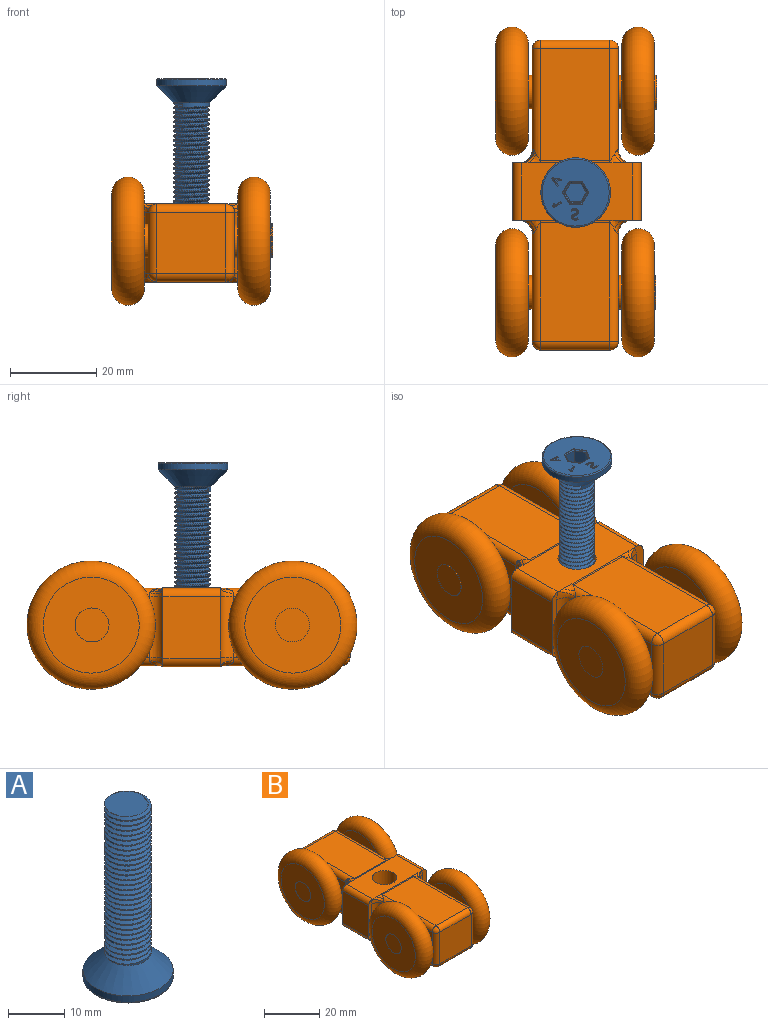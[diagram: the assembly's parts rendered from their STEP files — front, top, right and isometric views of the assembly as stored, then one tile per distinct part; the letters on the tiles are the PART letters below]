
ASSEMBLY  parts=2 mates=1
PART A: 134 faces, bbox 17.9x17.9x39 mm
  f0: plane 8.28x8.14mm, normal (0,0,1), area 47.4mm2, adj f4,f5,f7,f8
  f1: cylinder r=8.06mm len=16.12mm, axis (0,0,-1), area 70.4mm2, adj f3,f127
  f2: plane 15.61x15.61mm, normal (0,0,-1), area 159.1mm2, adj f49,f50,f51,f52,f53,f54,f55,f56
  f3: cone r=4.16mm half-angle=45deg, axis (0,0,-1), area 211.7mm2, adj f1,f4,f9
  f4: cylinder r=4.16mm len=32.5mm, axis (0,0,-1), area 180mm2, adj f0,f3,f5,f6,f7,f8
  f5: plane 0.02x0.01mm, normal (0.87,0.5,0), area 0mm2, adj f0,f4,f8
  f6: plane 0.84x0.63mm, normal (-0.87,-0.5,0), area 0.3mm2, adj f4,f7,f8,f9
  f7: bspline ~32.56x9.6mm, area 589mm2, adj f0,f4,f6,f8
  f8: bspline ~32.92x9.6mm, area 595.5mm2, adj f0,f4,f5,f6,f7,f9
  f9: cylinder r=4.16mm len=0.22mm, axis (0,0,-1), area 0mm2, adj f3,f6,f8
  f10: plane 3.14x2.29mm, normal (-0.86,0.5,0), area 8.3mm2, adj f11,f15,f22,f28
  f11: plane 3.14x2.31mm, normal (-0.87,-0.5,0), area 8.4mm2, adj f10,f12,f20,f26
  f12: plane 3.14x2.65mm, normal (0,-1,0), area 8.3mm2, adj f11,f13,f18,f24
  f13: plane 3.14x2.29mm, normal (0.86,-0.5,0), area 8.3mm2, adj f12,f14,f17,f23
  f14: plane 3.14x2.31mm, normal (0.87,0.5,0), area 8.4mm2, adj f13,f15,f19,f25
  f15: plane 3.14x2.65mm, normal (0,1,0), area 8.3mm2, adj f10,f14,f21,f27
  f16: plane 4.85x4.2mm, normal (0,0,-1), area 15.3mm2, adj f23,f24,f25,f26,f27,f28
  f17: plane 2.55x1.63mm, normal (0.61,-0.36,-0.71), area 1mm2, adj f13,f18,f19,f128
  f18: plane 2.95x0.26mm, normal (0,-0.71,-0.71), area 1mm2, adj f12,f17,f20,f130
  f19: plane 2.56x1.63mm, normal (0.61,0.35,-0.71), area 1mm2, adj f14,f17,f21,f129
  f20: plane 2.56x1.63mm, normal (-0.61,-0.35,-0.71), area 1mm2, adj f11,f18,f22,f132
  f21: plane 2.94x0.26mm, normal (0,0.71,-0.71), area 1mm2, adj f15,f19,f22,f131
  f22: plane 2.55x1.63mm, normal (-0.61,0.36,-0.71), area 1mm2, adj f10,f20,f21,f133
  f23: plane 2.29x1.45mm, normal (0.61,-0.36,-0.71), area 0.7mm2, adj f13,f16,f24,f25
  f24: plane 2.65x0.21mm, normal (0,-0.71,-0.71), area 0.7mm2, adj f12,f16,f23,f26
  f25: plane 2.31x1.45mm, normal (0.61,0.35,-0.71), area 0.7mm2, adj f14,f16,f23,f27
  f26: plane 2.31x1.45mm, normal (-0.61,-0.35,-0.71), area 0.7mm2, adj f11,f16,f24,f28
  f27: plane 2.65x0.21mm, normal (0,0.71,-0.71), area 0.7mm2, adj f15,f16,f25,f28
  f28: plane 2.29x1.45mm, normal (-0.61,0.36,-0.71), area 0.7mm2, adj f10,f16,f26,f27
  f29: plane 0.43x0.2mm, normal (-0.87,-0.5,0), area 0.1mm2, adj f30,f41,f42,f49
  f30: plane 1.65x1.32mm, normal (0.78,-0.62,0), area 0.9mm2, adj f29,f31,f42,f51
  f31: plane 0.43x0.17mm, normal (0.87,0.5,0), area 0.1mm2, adj f30,f32,f42,f53
  f32: plane 2.09x0.43mm, normal (-0.15,0.99,0), area 0.9mm2, adj f31,f33,f42,f55
  f33: plane 0.43x0.2mm, normal (-0.87,-0.5,0), area 0.1mm2, adj f32,f34,f42,f56
  f34: plane 0.66x0.43mm, normal (0.15,-0.99,0), area 0.3mm2, adj f33,f35,f42,f54
  f35: plane 0.68x0.43mm, normal (-0.87,-0.5,0), area 0.3mm2, adj f34,f41,f42,f52
  f36: plane 0.55x0.43mm, normal (0.87,0.5,0), area 0.3mm2, adj f37,f40,f42,f45
  f37: plane 0.64x0.43mm, normal (0.16,-0.99,0), area 0.3mm2, adj f36,f38,f42,f47
  f38: extruded ~0.43x0.29mm, area 0.1mm2, adj f37,f39,f42,f48
  f39: extruded ~0.43x0.22mm, area 0.1mm2, adj f38,f40,f42,f46
  f40: plane 0.5x0.43mm, normal (-0.77,0.63,0), area 0.3mm2, adj f36,f39,f42,f44
  f41: plane 0.52x0.43mm, normal (-0.78,0.62,0), area 0.3mm2, adj f29,f35,f42,f50
  f42: plane 2.18x1.81mm, normal (0,0,-1), area 1mm2, adj f29,f30,f31,f32,f33,f34,f35,f36
  f43: plane 0.57x0.45mm, normal (0,0,-1), area 0.1mm2, adj f44,f45,f47
  f44: plane 0.57x0.41mm, normal (-0.55,0.45,-0.71), area 0.1mm2, adj f40,f43,f45,f46
  f45: plane 0.55x0.33mm, normal (0.61,0.35,-0.71), area 0.1mm2, adj f36,f43,f44,f47
  f46: bspline ~0.27x0.26mm, area 0mm2, adj f39,f44,f48
  f47: plane 0.68x0.16mm, normal (0.11,-0.7,-0.71), area 0.1mm2, adj f37,f43,f45,f48
  f48: bspline ~0.34x0.15mm, area 0mm2, adj f38,f46,f47
  f49: plane 0.34x0.21mm, normal (-0.61,-0.35,-0.71), area 0mm2, adj f2,f29,f50,f51
  f50: plane 0.53x0.51mm, normal (-0.55,0.44,-0.71), area 0.1mm2, adj f2,f41,f49,f52
  f51: plane 1.78x1.42mm, normal (0.55,-0.44,-0.71), area 0.2mm2, adj f2,f30,f49,f53
  f52: plane 0.68x0.43mm, normal (-0.61,-0.35,-0.71), area 0.1mm2, adj f2,f35,f50,f54
  f53: plane 0.25x0.19mm, normal (0.61,0.35,-0.71), area 0mm2, adj f2,f31,f51,f55
  f54: plane 0.7x0.18mm, normal (0.11,-0.7,-0.71), area 0.1mm2, adj f2,f34,f52,f56
  f55: plane 2.25x0.39mm, normal (-0.1,0.7,-0.71), area 0.2mm2, adj f2,f32,f53,f56
  f56: plane 0.34x0.24mm, normal (-0.61,-0.35,-0.71), area 0mm2, adj f2,f33,f54,f55
  f57: plane 1.78x1.03mm, normal (-0.5,-0.87,0), area 0.9mm2, adj f58,f64,f65,f71
  f58: plane 0.43x0.17mm, normal (0.87,-0.5,0), area 0.1mm2, adj f57,f59,f65,f69
  f59: plane 0.68x0.43mm, normal (0.99,0.13,0), area 0.3mm2, adj f58,f60,f65,f67
  f60: plane 0.43x0.2mm, normal (-0.13,0.99,0), area 0.1mm2, adj f59,f61,f65,f68
  f61: extruded ~0.43x0.35mm, area 0.1mm2, adj f60,f65,f66,f70
  f62: extruded ~0.43x0.15mm, area 0.1mm2, adj f63,f65,f66,f74
  f63: plane 1.27x0.73mm, normal (0.5,0.87,0), area 0.6mm2, adj f62,f64,f65,f75
  f64: plane 0.43x0.2mm, normal (-0.87,0.5,0), area 0.1mm2, adj f57,f63,f65,f73
  f65: plane 1.88x1.23mm, normal (0,0,-1), area 0.6mm2, adj f57,f58,f59,f60,f61,f62,f63,f64
  f66: plane 0.43x0.11mm, normal (-0.56,0.83,0), area 0.1mm2, adj f61,f62,f65,f72
  f67: plane 0.78x0.17mm, normal (0.7,0.09,-0.71), area 0.1mm2, adj f2,f59,f68,f69
  f68: plane 0.35x0.11mm, normal (-0.09,0.7,-0.71), area 0mm2, adj f2,f60,f67,f70
  f69: plane 0.27x0.18mm, normal (0.61,-0.35,-0.71), area 0mm2, adj f2,f58,f67,f71
  f70: bspline ~0.48x0.15mm, area 0mm2, adj f2,f61,f68,f72
  f71: plane 1.91x1.13mm, normal (-0.35,-0.61,-0.71), area 0.2mm2, adj f2,f57,f69,f73
  f72: plane 0.11x0.11mm, normal (-0.39,0.59,-0.71), area 0mm2, adj f66,f70,f74
  f73: plane 0.33x0.22mm, normal (-0.61,0.35,-0.71), area 0mm2, adj f2,f64,f71,f75
  f74: bspline ~0.19x0.16mm, area 0mm2, adj f2,f62,f72,f75
  f75: plane 1.34x0.84mm, normal (0.35,0.61,-0.71), area 0.2mm2, adj f2,f63,f73,f74
  f76: extruded ~0.43x0.4mm, area 0.2mm2, adj f77,f100,f101,f111
  f77: extruded ~0.52x0.43mm, area 0.3mm2, adj f76,f78,f101,f113
  f78: extruded ~0.43x0.34mm, area 0.2mm2, adj f77,f79,f101,f115
  f79: extruded ~0.43x0.16mm, area 0.1mm2, adj f78,f80,f101,f117
  f80: extruded ~0.43x0.21mm, area 0.1mm2, adj f79,f81,f101,f119
  f81: extruded ~0.43x0.27mm, area 0.1mm2, adj f80,f82,f101,f121
  f82: extruded ~0.43x0.35mm, area 0.2mm2, adj f81,f83,f101,f123
  f83: extruded ~0.58x0.43mm, area 0.3mm2, adj f82,f84,f101,f125
  f84: plane 0.43x0.24mm, normal (-0.94,0.34,0), area 0.1mm2, adj f83,f85,f101,f126
  f85: extruded ~0.66x0.43mm, area 0.3mm2, adj f84,f86,f101,f124
  f86: extruded ~0.55x0.43mm, area 0.3mm2, adj f85,f87,f101,f122
  f87: extruded ~0.44x0.43mm, area 0.2mm2, adj f86,f88,f101,f120
  f88: extruded ~0.43x0.43mm, area 0.2mm2, adj f87,f89,f101,f118
  f89: extruded ~0.48x0.43mm, area 0.2mm2, adj f88,f90,f101,f116
  f90: extruded ~0.43x0.36mm, area 0.2mm2, adj f89,f91,f101,f114
  f91: extruded ~0.43x0.17mm, area 0.1mm2, adj f90,f92,f101,f112
  f92: extruded ~0.43x0.21mm, area 0.1mm2, adj f91,f93,f101,f110
  f93: extruded ~0.43x0.3mm, area 0.1mm2, adj f92,f94,f101,f108
  f94: extruded ~0.43x0.42mm, area 0.2mm2, adj f93,f95,f101,f106
  f95: extruded ~0.43x0.35mm, area 0.1mm2, adj f94,f96,f101,f104
  f96: extruded ~0.43x0.32mm, area 0.1mm2, adj f95,f97,f101,f102
  f97: plane 0.43x0.27mm, normal (1,0,0), area 0.1mm2, adj f96,f98,f101,f103
  f98: extruded ~0.66x0.43mm, area 0.3mm2, adj f97,f99,f101,f105
  f99: extruded ~0.63x0.43mm, area 0.3mm2, adj f98,f100,f101,f107
  f100: extruded ~0.5x0.43mm, area 0.2mm2, adj f76,f99,f101,f109
  f101: plane 2.48x1.52mm, normal (0,0,-1), area 1.3mm2, adj f76,f77,f78,f79,f80,f81,f82,f83
  f102: bspline ~0.46x0.22mm, area 0mm2, adj f2,f96,f103,f104
  f103: plane 0.43x0.08mm, normal (0.71,0,-0.71), area 0mm2, adj f2,f97,f102,f105
  f104: bspline ~0.35x0.11mm, area 0mm2, adj f2,f95,f102,f106
  f105: bspline ~0.74x0.21mm, area 0.1mm2, adj f2,f98,f103,f107
  f106: bspline ~0.42x0.17mm, area 0mm2, adj f2,f94,f104,f108
  f107: bspline ~0.67x0.25mm, area 0.1mm2, adj f2,f99,f105,f109
  f108: bspline ~0.3x0.19mm, area 0mm2, adj f2,f93,f106,f110
  f109: bspline ~0.56x0.31mm, area 0.1mm2, adj f2,f100,f107,f111
  f110: bspline ~0.21x0.11mm, area 0mm2, adj f2,f92,f108,f112
  f111: bspline ~0.45x0.22mm, area 0mm2, adj f2,f76,f109,f113
  f112: bspline ~0.21x0.19mm, area 0mm2, adj f2,f91,f110,f114
  f113: bspline ~0.58x0.36mm, area 0.1mm2, adj f2,f77,f111,f115
  f114: bspline ~0.38x0.22mm, area 0mm2, adj f2,f90,f112,f116
  f115: bspline ~0.36x0.21mm, area 0mm2, adj f2,f78,f113,f117
  f116: bspline ~0.54x0.36mm, area 0.1mm2, adj f2,f89,f114,f118
  f117: bspline ~0.2x0.18mm, area 0mm2, adj f2,f79,f115,f119
  f118: bspline ~0.48x0.22mm, area 0.1mm2, adj f2,f88,f116,f120
  f119: bspline ~0.21x0.11mm, area 0mm2, adj f2,f80,f117,f121
  f120: bspline ~0.5x0.29mm, area 0.1mm2, adj f2,f87,f118,f122
  f121: bspline ~0.27x0.18mm, area 0mm2, adj f2,f81,f119,f123
  f122: bspline ~0.6x0.24mm, area 0.1mm2, adj f2,f86,f120,f124
  f123: bspline ~0.35x0.16mm, area 0mm2, adj f2,f82,f121,f125
  f124: bspline ~0.76x0.23mm, area 0.1mm2, adj f2,f85,f122,f126
  f125: bspline ~0.65x0.22mm, area 0.1mm2, adj f2,f83,f123,f126
  f126: plane 0.39x0.18mm, normal (-0.67,0.24,-0.71), area 0mm2, adj f2,f84,f124,f125
  f127: torus R=7.76mm, axis (0,0,1), area 23.5mm2, adj f1,f2
  f128: cylinder r=0.15mm len=2.71mm, axis (-0.5,-0.86,0), area 0.4mm2, adj f2,f17,f129,f130
  f129: cylinder r=0.15mm len=2.72mm, axis (0.5,-0.87,0), area 0.4mm2, adj f2,f19,f128,f131
  f130: cylinder r=0.15mm len=3.07mm, axis (-1,0,0), area 0.4mm2, adj f2,f18,f128,f132
  f131: cylinder r=0.15mm len=3.07mm, axis (1,0,0), area 0.4mm2, adj f2,f21,f129,f133
  f132: cylinder r=0.15mm len=2.72mm, axis (-0.5,0.87,0), area 0.4mm2, adj f2,f20,f130,f133
  f133: cylinder r=0.15mm len=2.71mm, axis (0.5,0.86,0), area 0.4mm2, adj f2,f22,f131,f132
PART B: 100 faces, bbox 38x79.5x32.9 mm
  f0: bspline ~2.7x2.53mm, area 1.8mm2, adj f1,f14,f19,f69
  f1: bspline ~3.2x2.76mm, area 1.2mm2, adj f0,f2,f14,f19
  f2: bspline ~3.29x2.98mm, area 2.3mm2, adj f1,f14,f17,f66
  f3: bspline ~3.51x3mm, area 3.6mm2, adj f12,f19,f73,f75
  f4: plane 18.23x2.82mm, normal (0,1,0), area 40.7mm2, adj f19,f20,f31,f44,f45,f74,f75,f76
  f5: bspline ~3.51x3mm, area 3.6mm2, adj f19,f26,f34,f36
  f6: bspline ~3.51x3mm, area 3.6mm2, adj f19,f24,f40,f42
  f7: plane 18.23x2.07mm, normal (0,-1,0), area 27.2mm2, adj f20,f21,f41,f42,f43,f46,f47
  f8: cylinder r=2mm len=25.23mm, axis (0,1,0), area 75.5mm2, adj f9,f15,f59,f67,f68
  f9: plane 25.23x15.98mm, normal (0,0,-1), area 403mm2, adj f8,f10,f61,f70
  f10: cylinder r=2mm len=25.23mm, axis (0,1,0), area 75.5mm2, adj f9,f11,f63,f72,f74
  f11: plane 23.41x13.95mm, normal (1,0,0), area 277.9mm2, adj f10,f12,f62,f76,f96
  f12: cylinder r=2mm len=25.96mm, axis (0,1,0), area 76.1mm2, adj f3,f11,f13,f60,f73,f75
  f13: plane 25.96x15.98mm, normal (0,0,1), area 414.7mm2, adj f12,f14,f58,f71
  f14: cylinder r=2mm len=25.96mm, axis (0,1,0), area 75.9mm2, adj f0,f1,f2,f13,f15,f56,f66,f69
  f15: plane 23.41x13.95mm, normal (-1,0,0), area 277.9mm2, adj f8,f14,f57,f65,f93
  f16: plane 15.98x13.95mm, normal (0,1,0), area 222.9mm2, adj f57,f58,f61,f62
  f17: plane 18.24x2.09mm, normal (0,1,0), area 27.3mm2, adj f2,f20,f21,f46,f47,f65,f66,f67
  f18: plane 18.23x2.82mm, normal (0,-1,0), area 40.7mm2, adj f19,f20,f31,f32,f33,f34,f44,f45
  f19: plane 26.4x13.92mm, normal (0,0,1), area 282.7mm2, adj f0,f1,f3,f4,f5,f6,f18,f36
  f20: plane 26.52x14.05mm, normal (0,0,-1), area 282.7mm2, adj f4,f7,f17,f18,f35,f37,f39,f45
  f21: plane 14.23x13.33mm, normal (-1,0,0), area 189.7mm2, adj f7,f17,f46,f47
  f22: plane 15.98x13.95mm, normal (0,-1,0), area 222.9mm2, adj f49,f50,f53,f54
  f23: plane 24.96x13.95mm, normal (-1,0,0), area 299.7mm2, adj f24,f30,f43,f54,f81
  f24: cylinder r=2mm len=27.52mm, axis (0,1,0), area 81mm2, adj f6,f23,f25,f40,f42,f55
  f25: plane 27.52x15.98mm, normal (0,0,1), area 439.6mm2, adj f24,f26,f38,f53
  f26: cylinder r=2mm len=27.52mm, axis (0,1,0), area 81mm2, adj f5,f25,f27,f34,f36,f51
  f27: plane 24.96x13.95mm, normal (1,0,0), area 299.7mm2, adj f26,f28,f32,f49,f84
  f28: cylinder r=2mm len=26.79mm, axis (0,1,0), area 80.4mm2, adj f27,f29,f33,f35,f48
  f29: plane 26.79x15.98mm, normal (0,0,-1), area 427.9mm2, adj f28,f30,f37,f50
  f30: cylinder r=2mm len=26.79mm, axis (0,1,0), area 80.4mm2, adj f23,f29,f39,f41,f52
  f31: plane 14.23x13.33mm, normal (1,0,0), area 189.7mm2, adj f4,f18,f44,f45
  f32: cylinder r=3mm len=13.95mm, axis (0,0,1), area 65.7mm2, adj f18,f27,f33,f34
  f33: torus R=5mm, axis (0,1,0), area 6.8mm2, adj f18,f28,f32,f35
  f34: torus R=5mm, axis (0,1,0), area 6.1mm2, adj f5,f18,f26,f32
  f35: bspline ~4.76x3mm, area 6.9mm2, adj f20,f28,f33,f37
  f36: bspline ~3.47x2.47mm, area 2.8mm2, adj f5,f19,f26,f38
  f37: cylinder r=3mm len=15.98mm, axis (1,0,0), area 19.3mm2, adj f20,f29,f35,f39
  f38: cylinder r=3mm len=15.98mm, axis (1,0,0), area 7.1mm2, adj f19,f25,f36,f40
  f39: bspline ~4.76x3mm, area 6.9mm2, adj f20,f30,f37,f41
  f40: bspline ~3.47x2.47mm, area 2.8mm2, adj f6,f19,f24,f38
  f41: torus R=5mm, axis (0,1,0), area 6.8mm2, adj f7,f30,f39,f43
  f42: torus R=5mm, axis (0,1,0), area 6mm2, adj f6,f7,f24,f43
  f43: cylinder r=3mm len=13.95mm, axis (0,0,-1), area 65.7mm2, adj f7,f23,f41,f42
  f44: cylinder r=2mm len=13.33mm, axis (0,-1,0), area 41.9mm2, adj f4,f18,f19,f31
  f45: cylinder r=2mm len=13.33mm, axis (0,1,0), area 41.9mm2, adj f4,f18,f20,f31
  f46: cylinder r=2mm len=13.33mm, axis (0,1,0), area 41.9mm2, adj f7,f17,f19,f21
  f47: cylinder r=2mm len=13.33mm, axis (0,-1,0), area 41.9mm2, adj f7,f17,f20,f21
  f48: sphere r=2mm, area 4mm2, adj f28,f49,f50
  f49: cylinder r=2mm len=13.95mm, axis (0,0,-1), area 43.8mm2, adj f22,f27,f48,f51
  f50: cylinder r=2mm len=15.98mm, axis (-1,0,0), area 50.2mm2, adj f22,f29,f48,f52
  f51: sphere r=2mm, area 8.6mm2, adj f26,f49,f53
  f52: sphere r=2mm, area 6.3mm2, adj f30,f50,f54
  f53: cylinder r=2mm len=15.98mm, axis (1,0,0), area 50.2mm2, adj f22,f25,f51,f55
  f54: cylinder r=2mm len=13.95mm, axis (0,0,1), area 43.8mm2, adj f22,f23,f52,f55
  f55: sphere r=2mm, area 6.3mm2, adj f24,f53,f54
  f56: sphere r=2mm, area 6.3mm2, adj f14,f57,f58
  f57: cylinder r=2mm len=13.95mm, axis (0,0,-1), area 43.8mm2, adj f15,f16,f56,f59
  f58: cylinder r=2mm len=15.98mm, axis (-1,0,0), area 50.2mm2, adj f13,f16,f56,f60
  f59: sphere r=2mm, area 6.3mm2, adj f8,f57,f61
  f60: sphere r=2mm, area 8.6mm2, adj f12,f58,f62
  f61: cylinder r=2mm len=15.98mm, axis (1,0,0), area 50.2mm2, adj f9,f16,f59,f63
  f62: cylinder r=2mm len=13.95mm, axis (0,0,1), area 43.8mm2, adj f11,f16,f60,f63
  f63: sphere r=2mm, area 4mm2, adj f10,f61,f62
  f64: cylinder r=4.42mm len=18.23mm, axis (0,0,1), area 505.7mm2, adj f19,f20
  f65: cylinder r=3mm len=13.95mm, axis (0,0,1), area 65.7mm2, adj f15,f17,f66,f67
  f66: bspline ~3.23x3mm, area 4.3mm2, adj f2,f14,f17,f65
  f67: torus R=5mm, axis (0,1,0), area 6.8mm2, adj f8,f17,f65,f68
  f68: bspline ~4.76x3mm, area 6.9mm2, adj f8,f20,f67,f70
  f69: bspline ~3.55x2.51mm, area 2.8mm2, adj f0,f14,f19,f71
  f70: cylinder r=3mm len=15.98mm, axis (1,0,0), area 19.3mm2, adj f9,f20,f68,f72
  f71: cylinder r=3mm len=15.98mm, axis (1,0,0), area 7.1mm2, adj f13,f19,f69,f73
  f72: bspline ~4.76x3mm, area 6.9mm2, adj f10,f20,f70,f74
  f73: bspline ~3.47x2.47mm, area 2.8mm2, adj f3,f12,f19,f71
  f74: torus R=5mm, axis (0,1,0), area 6.8mm2, adj f4,f10,f72,f76
  f75: torus R=5mm, axis (0,1,0), area 6.1mm2, adj f3,f4,f12,f76
  f76: cylinder r=3mm len=13.95mm, axis (0,0,-1), area 65.7mm2, adj f4,f11,f74,f75
  f77: plane 7.88x7.88mm, normal (-1,0,0), area 48.6mm2, adj f78
  f78: plane 22.22x22.22mm, normal (-1,0,0), area 338.8mm2, adj f77,f79
  f79: torus R=11.1mm, axis (1,0,0), area 998.7mm2, adj f78,f80
  f80: plane 22.21x22.21mm, normal (1,0,0), area 338.8mm2, adj f79,f81
  f81: cylinder r=3.93mm len=7.87mm, axis (-1,0,0), area 22.8mm2, adj f23,f80
  f82: plane 7.87x7.87mm, normal (1,0,0), area 48.6mm2, adj f83
  f83: cylinder r=3.93mm len=7.87mm, axis (-1,0,0), area 8.1mm2, adj f82,f86
  f84: cylinder r=3.93mm len=7.87mm, axis (-1,0,0), area 19.3mm2, adj f27,f87
  f85: torus R=11.1mm, axis (1,0,0), area 998.7mm2, adj f86,f87
  f86: plane 22.21x22.21mm, normal (1,0,0), area 338.8mm2, adj f83,f85
  f87: plane 22.21x22.21mm, normal (-1,0,0), area 338.8mm2, adj f84,f85
  f88: plane 7.87x7.87mm, normal (-1,0,0), area 48.6mm2, adj f89
  f89: cylinder r=3.93mm len=7.87mm, axis (-1,0,0), area 1.7mm2, adj f88,f90
  f90: plane 22.21x22.21mm, normal (-1,0,0), area 338.8mm2, adj f89,f91
  f91: torus R=11.1mm, axis (1,0,0), area 998.7mm2, adj f90,f92
  f92: plane 22.21x22.21mm, normal (1,0,0), area 338.8mm2, adj f91,f93
  f93: cylinder r=3.93mm len=7.87mm, axis (-1,0,0), area 22.8mm2, adj f15,f92
  f94: plane 7.87x7.87mm, normal (1,0,0), area 48.6mm2, adj f95
  f95: cylinder r=3.93mm len=7.87mm, axis (-1,0,0), area 12.4mm2, adj f94,f98
  f96: cylinder r=3.93mm len=7.87mm, axis (-1,0,0), area 19.3mm2, adj f11,f99
  f97: torus R=11.1mm, axis (1,0,0), area 998.7mm2, adj f98,f99
  f98: plane 22.21x22.21mm, normal (1,0,0), area 338.8mm2, adj f95,f97
  f99: plane 22.21x22.21mm, normal (-1,0,0), area 338.8mm2, adj f96,f97
PLACE A rot(axis=(1,0,0),180deg) t=(0.03,-0.14,37.47)mm
PLACE B t=(-0.2,0,0)mm
MATE revolute A.f1 <-> B.f64  axis (0,0,-1) through (0.03,-0.14,-0.62)mm
